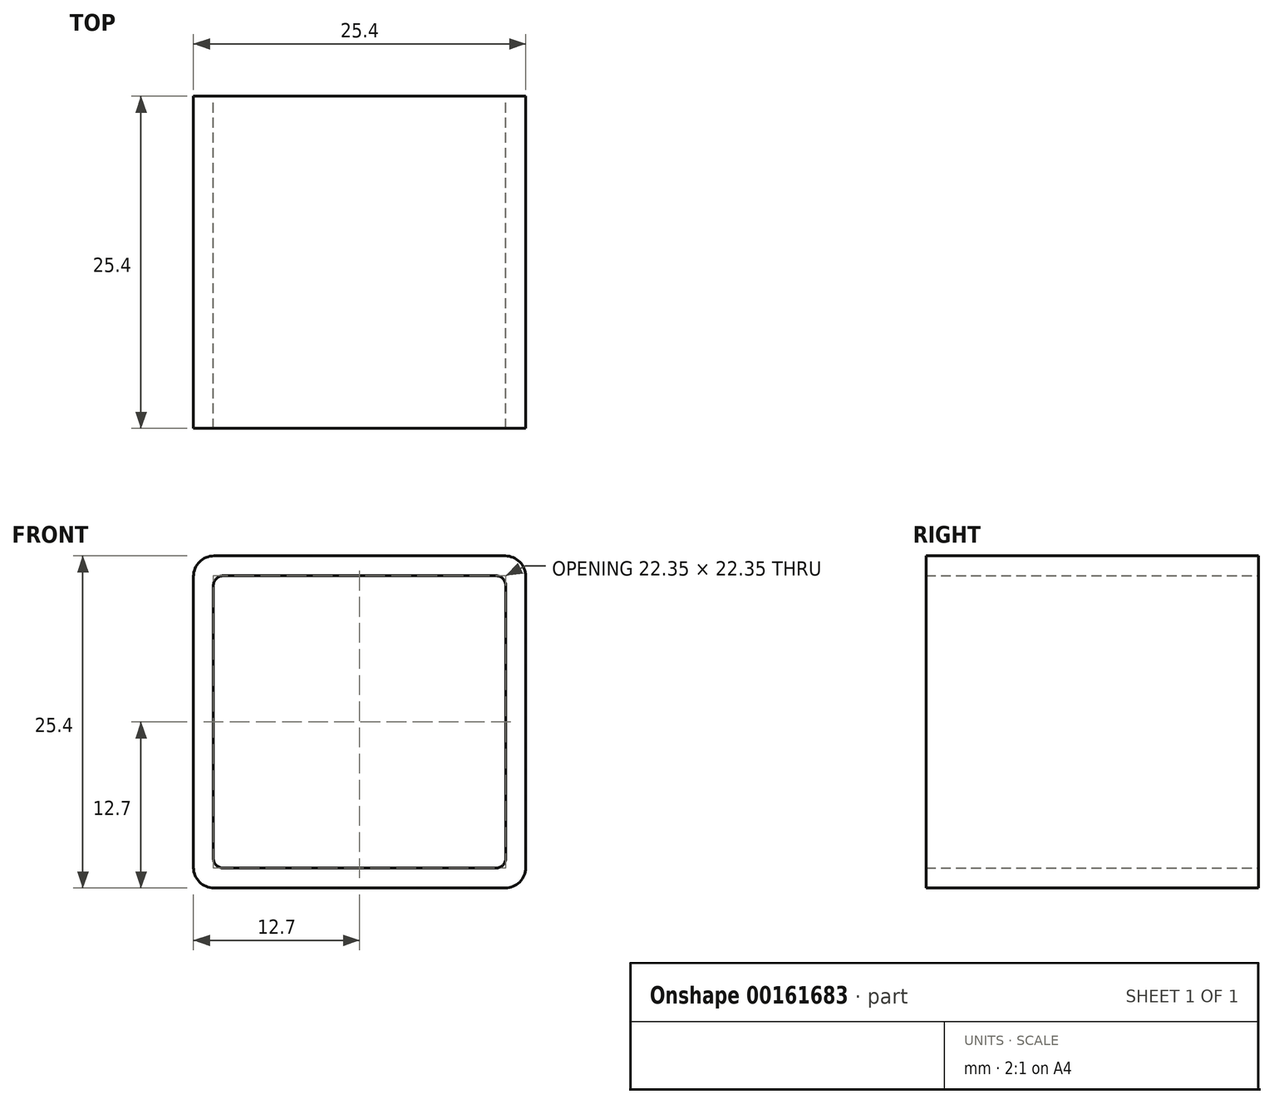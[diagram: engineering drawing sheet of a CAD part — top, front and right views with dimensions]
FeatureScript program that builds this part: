
annotation { "Feature Type Name" : "Feature", "Feature Type Description" : "" }
export const myFeature = defineFeature(function(context is Context, id is Id, definition is map)
    precondition{}
    {
        {
            var Q0;
            Q0=qCreatedBy(makeId("Front.planeOp"),FACE);
            var sketch = newSketch(context, id + "F0", { "sketchPlane" : qUnion([Q0])});
            skLineSegment(sketch, "E0.bottom", {"start": v(1.57, 0) * mm, "end": v(23.83, 0) * mm});
            skLineSegment(sketch, "E0.top", {"start": v(1.57, 25.4) * mm, "end": v(23.83, 25.4) * mm});
            skLineSegment(sketch, "E0.left", {"start": v(0, 1.57) * mm, "end": v(0, 23.83) * mm});
            skLineSegment(sketch, "E0.right", {"start": v(25.4, 1.57) * mm, "end": v(25.4, 23.83) * mm});
            skPoint(sketch, "E1.visualSharp", {"position": v(0, 25.4) * mm});
            skArc(sketch, "E1.filletArc", {"start": v(1.57, 25.4) * mm, "mid": v(0.46, 24.94) * mm, "end": v(0, 23.83) * mm});
            skPoint(sketch, "E2.visualSharp", {"position": v(25.4, 25.4) * mm});
            skArc(sketch, "E2.filletArc", {"start": v(25.4, 23.83) * mm, "mid": v(24.94, 24.94) * mm, "end": v(23.83, 25.4) * mm});
            skPoint(sketch, "E3.visualSharp", {"position": v(25.4, 0) * mm});
            skArc(sketch, "E3.filletArc", {"start": v(23.83, 0) * mm, "mid": v(24.94, 0.46) * mm, "end": v(25.4, 1.57) * mm});
            skPoint(sketch, "E4.visualSharp", {"position": v(0, 0) * mm});
            skArc(sketch, "E4.filletArc", {"start": v(0, 1.57) * mm, "mid": v(0.46, 0.46) * mm, "end": v(1.57, 0) * mm});
            skLineSegment(sketch, "E5.0", {"start": v(2.29, 23.88) * mm, "end": v(23.11, 23.88) * mm});
            skLineSegment(sketch, "E6.0", {"start": v(1.52, 2.29) * mm, "end": v(1.52, 23.11) * mm});
            skLineSegment(sketch, "E7.0", {"start": v(23.88, 2.29) * mm, "end": v(23.88, 23.11) * mm});
            skLineSegment(sketch, "E8.0", {"start": v(2.29, 1.52) * mm, "end": v(23.11, 1.52) * mm});
            skArc(sketch, "E9.filletArc", {"start": v(2.29, 23.88) * mm, "mid": v(1.75, 23.65) * mm, "end": v(1.52, 23.11) * mm});
            skArc(sketch, "E10.filletArc", {"start": v(1.52, 2.29) * mm, "mid": v(1.75, 1.75) * mm, "end": v(2.29, 1.52) * mm});
            skArc(sketch, "E11.filletArc", {"start": v(23.11, 1.52) * mm, "mid": v(23.65, 1.75) * mm, "end": v(23.88, 2.29) * mm});
            skArc(sketch, "E12.filletArc", {"start": v(23.88, 23.11) * mm, "mid": v(23.65, 23.65) * mm, "end": v(23.11, 23.88) * mm});
            skSolve(sketch);
        }
        {
            var Q0;
            Q0=makeQuery(id+"F0.imprint","IMPRINT",FACE,{"disambiguationData":[TD([[makeQuery(id+"F0.imprint","IMPRINT",EDGE,{"derivedFrom":sQuery(id+"F0.wireOp",EDGE,"E0.bottom")}),1.0]])]});
            extrude(context, id + "F1", {"entities" : qUnion([Q0]), "depth" : 25.4 * mm});
        }
    });
